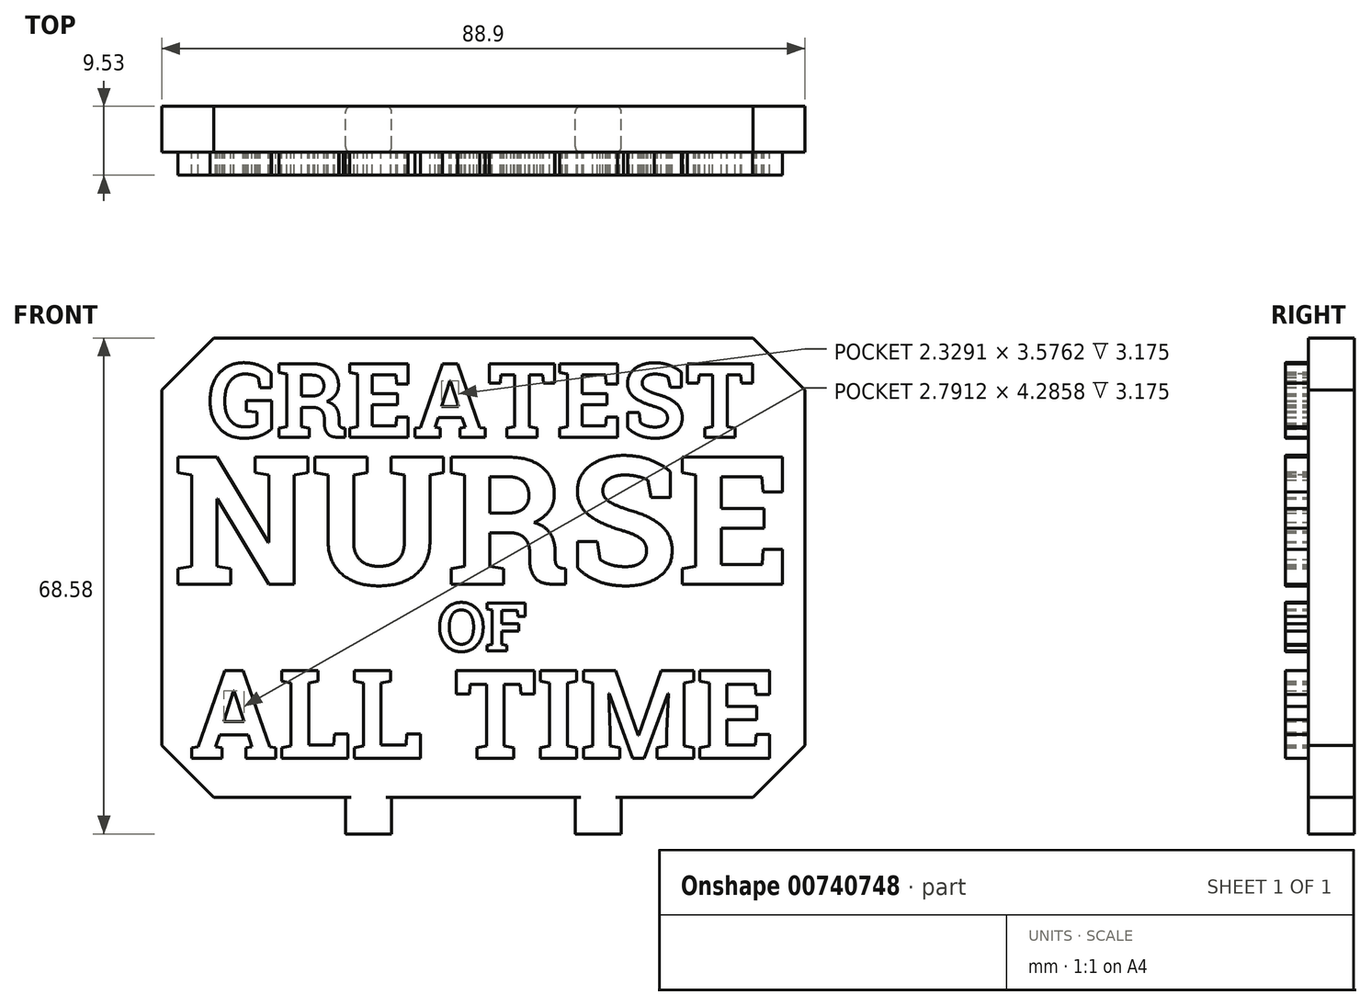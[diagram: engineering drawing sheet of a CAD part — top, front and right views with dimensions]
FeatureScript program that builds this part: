
annotation { "Feature Type Name" : "Feature", "Feature Type Description" : "" }
export const myFeature = defineFeature(function(context is Context, id is Id, definition is map)
    precondition{}
    {
        {
            var Q0;
            Q0=qCreatedBy(makeId("Front.planeOp"),FACE);
            var sketch = newSketch(context, id + "F0", { "sketchPlane" : qUnion([Q0])});
            skLineSegment(sketch, "E0.bottom", {"start": v(0, 0) * mm, "end": v(88.9, 0) * mm});
            skLineSegment(sketch, "E0.top", {"start": v(0, 63.5) * mm, "end": v(88.9, 63.5) * mm});
            skLineSegment(sketch, "E0.left", {"start": v(0, 0) * mm, "end": v(0, 63.5) * mm});
            skLineSegment(sketch, "E0.right", {"start": v(88.9, 0) * mm, "end": v(88.9, 63.5) * mm});
            skPoint(sketch, "E1", {"position": v(1.57, 38.36) * mm});
            skLineSegment(sketch, "E2", {"start": v(0, 56.32) * mm, "end": v(7.18, 63.5) * mm});
            skLineSegment(sketch, "E3", {"start": v(81.72, 63.5) * mm, "end": v(88.9, 56.32) * mm});
            skLineSegment(sketch, "E4", {"start": v(81.72, 0) * mm, "end": v(88.9, 7.18) * mm});
            skLineSegment(sketch, "E5", {"start": v(0, 7.18) * mm, "end": v(7.18, 0) * mm});
            skSolve(sketch);
        }
        {
            var Q0;
            {var subQ3=sQuery(id+"F0.wireOp",EDGE,"E2");Q0=makeQuery(id+"F0.imprint","IMPRINT",FACE,{"disambiguationData":[TD([[makeQuery(id+"F0.imprint","IMPRINT",EDGE,{"derivedFrom":subQ3}),-1.0]])]});}
            extrude(context, id + "F1", {"entities" : qUnion([Q0]), "depth" : 6.35 * mm, "offsetDistance" : 25.4 * mm});
        }
        {
            var Q0;
            Q0=makeQuery(id+"F1.opExtrude","CAP_FACE",FACE,{"disambiguationData":[OSD([sQuery(id+"F0.wireOp",EDGE,"E0.bottom"),sQuery(id+"F0.wireOp",EDGE,"E0.top"),sQuery(id+"F0.wireOp",EDGE,"E0.left"),sQuery(id+"F0.wireOp",EDGE,"E0.right"),sQuery(id+"F0.wireOp",EDGE,"E2"),sQuery(id+"F0.wireOp",EDGE,"E3"),sQuery(id+"F0.wireOp",EDGE,"E4"),sQuery(id+"F0.wireOp",EDGE,"E5")])],"isStart":false});
            var sketch = newSketch(context, id + "F2", { "sketchPlane" : qUnion([Q0])});
            skLineSegment(sketch, "E6.bottom", {"start": v(0, 0) * mm, "end": v(88.9, 0) * mm});
            skLineSegment(sketch, "E6.top", {"start": v(0, 63.5) * mm, "end": v(88.9, 63.5) * mm});
            skLineSegment(sketch, "E6.left", {"start": v(0, 0) * mm, "end": v(0, 63.5) * mm});
            skLineSegment(sketch, "E6.right", {"start": v(88.9, 0) * mm, "end": v(88.9, 63.5) * mm});
            skText(sketch, "E7", { "text": "GREATEST", "fontName": "RobotoSlab-Bold.ttf"});
            skText(sketch, "E8", { "text": "NURSE", "fontName": "RobotoSlab-Bold.ttf"});
            skText(sketch, "E9", { "text": "OF", "fontName": "RobotoSlab-Bold.ttf"});
            skText(sketch, "E10", { "text": "ALL TIME", "fontName": "RobotoSlab-Bold.ttf"});
            skPoint(sketch, "E11", {"position": v(1.57, 38.36) * mm});
            skLineSegment(sketch, "E12", {"start": v(0, 56.32) * mm, "end": v(7.18, 63.5) * mm});
            skLineSegment(sketch, "E13", {"start": v(81.72, 63.5) * mm, "end": v(88.9, 56.32) * mm});
            skLineSegment(sketch, "E14", {"start": v(81.72, 0) * mm, "end": v(88.9, 7.18) * mm});
            skLineSegment(sketch, "E15", {"start": v(0, 7.18) * mm, "end": v(7.18, 0) * mm});
            const initialGuessF2  = {"E7": [0.00635, 0.04979, 1, 0, 0.01028], "E8": [0.00157, 0.02947, 1, 0, 0.01778], "E9": [0.0381, 0.02021, 1, 0, 0.00672], "E10": [0.0038, 0.00535, 1, 0, 0.01232]};
            skSetInitialGuess(sketch, initialGuessF2);
            skSolve(sketch);
        }
        {
            var Q0;
            Q0=makeQuery(id+"F2.imprint","IMPRINT",FACE,{"disambiguationData":[TD([[makeQuery(id+"F2.imprint","IMPRINT",EDGE,{"derivedFrom":sQuery(id+"F2.wireOp",EDGE,"E7.sketch_text.stroke-0")}),-1.0]])]});
            var Q1;
            Q1=makeQuery(id+"F2.imprint","IMPRINT",FACE,{"disambiguationData":[TD([[makeQuery(id+"F2.imprint","IMPRINT",EDGE,{"derivedFrom":sQuery(id+"F2.wireOp",EDGE,"E7.sketch_text.stroke-26")}),-1.0]])]});
            var Q2;
            Q2=makeQuery(id+"F2.imprint","IMPRINT",FACE,{"disambiguationData":[TD([[makeQuery(id+"F2.imprint","IMPRINT",EDGE,{"derivedFrom":sQuery(id+"F2.wireOp",EDGE,"E7.sketch_text.stroke-62")}),-1.0]])]});
            var Q3;
            Q3=makeQuery(id+"F2.imprint","IMPRINT",FACE,{"disambiguationData":[TD([[makeQuery(id+"F2.imprint","IMPRINT",EDGE,{"derivedFrom":sQuery(id+"F2.wireOp",EDGE,"E7.sketch_text.stroke-83")}),-1.0]])]});
            var Q4;
            Q4=makeQuery(id+"F2.imprint","IMPRINT",FACE,{"disambiguationData":[TD([[makeQuery(id+"F2.imprint","IMPRINT",EDGE,{"derivedFrom":sQuery(id+"F2.wireOp",EDGE,"E7.sketch_text.stroke-103")}),-1.0]])]});
            var Q5;
            Q5=makeQuery(id+"F2.imprint","IMPRINT",FACE,{"disambiguationData":[TD([[makeQuery(id+"F2.imprint","IMPRINT",EDGE,{"derivedFrom":sQuery(id+"F2.wireOp",EDGE,"E7.sketch_text.stroke-119")}),-1.0]])]});
            var Q6;
            Q6=makeQuery(id+"F2.imprint","IMPRINT",FACE,{"disambiguationData":[TD([[makeQuery(id+"F2.imprint","IMPRINT",EDGE,{"derivedFrom":sQuery(id+"F2.wireOp",EDGE,"E7.sketch_text.stroke-140")}),-1.0]])]});
            var Q7;
            Q7=makeQuery(id+"F2.imprint","IMPRINT",FACE,{"disambiguationData":[TD([[makeQuery(id+"F2.imprint","IMPRINT",EDGE,{"derivedFrom":sQuery(id+"F2.wireOp",EDGE,"E7.sketch_text.stroke-170")}),-1.0]])]});
            var Q8;
            Q8=makeQuery(id+"F2.imprint","IMPRINT",FACE,{"disambiguationData":[TD([[makeQuery(id+"F2.imprint","IMPRINT",EDGE,{"derivedFrom":sQuery(id+"F2.wireOp",EDGE,"E8.sketch_text.stroke-0")}),-1.0]])]});
            var Q9;
            Q9=makeQuery(id+"F2.imprint","IMPRINT",FACE,{"disambiguationData":[TD([[makeQuery(id+"F2.imprint","IMPRINT",EDGE,{"derivedFrom":sQuery(id+"F2.wireOp",EDGE,"E8.sketch_text.stroke-24")}),-1.0]])]});
            var Q10;
            Q10=makeQuery(id+"F2.imprint","IMPRINT",FACE,{"disambiguationData":[TD([[makeQuery(id+"F2.imprint","IMPRINT",EDGE,{"derivedFrom":sQuery(id+"F2.wireOp",EDGE,"E8.sketch_text.stroke-48")}),-1.0]])]});
            var Q11;
            Q11=makeQuery(id+"F2.imprint","IMPRINT",FACE,{"disambiguationData":[TD([[makeQuery(id+"F2.imprint","IMPRINT",EDGE,{"derivedFrom":sQuery(id+"F2.wireOp",EDGE,"E8.sketch_text.stroke-84")}),-1.0]])]});
            var Q12;
            Q12=makeQuery(id+"F2.imprint","IMPRINT",FACE,{"disambiguationData":[TD([[makeQuery(id+"F2.imprint","IMPRINT",EDGE,{"derivedFrom":sQuery(id+"F2.wireOp",EDGE,"E8.sketch_text.stroke-114")}),-1.0]])]});
            var Q13;
            Q13=makeQuery(id+"F2.imprint","IMPRINT",FACE,{"disambiguationData":[TD([[makeQuery(id+"F2.imprint","IMPRINT",EDGE,{"derivedFrom":sQuery(id+"F2.wireOp",EDGE,"E9.sketch_text.stroke-0")}),-1.0]])]});
            var Q14;
            Q14=makeQuery(id+"F2.imprint","IMPRINT",FACE,{"disambiguationData":[TD([[makeQuery(id+"F2.imprint","IMPRINT",EDGE,{"derivedFrom":sQuery(id+"F2.wireOp",EDGE,"E9.sketch_text.stroke-20")}),-1.0]])]});
            var Q15;
            Q15=makeQuery(id+"F2.imprint","IMPRINT",FACE,{"disambiguationData":[TD([[makeQuery(id+"F2.imprint","IMPRINT",EDGE,{"derivedFrom":sQuery(id+"F2.wireOp",EDGE,"E10.sketch_text.stroke-0")}),-1.0]])]});
            var Q16;
            Q16=makeQuery(id+"F2.imprint","IMPRINT",FACE,{"disambiguationData":[TD([[makeQuery(id+"F2.imprint","IMPRINT",EDGE,{"derivedFrom":sQuery(id+"F2.wireOp",EDGE,"E10.sketch_text.stroke-20")}),-1.0]])]});
            var Q17;
            Q17=makeQuery(id+"F2.imprint","IMPRINT",FACE,{"disambiguationData":[TD([[makeQuery(id+"F2.imprint","IMPRINT",EDGE,{"derivedFrom":sQuery(id+"F2.wireOp",EDGE,"E10.sketch_text.stroke-36")}),-1.0]])]});
            var Q18;
            Q18=makeQuery(id+"F2.imprint","IMPRINT",FACE,{"disambiguationData":[TD([[makeQuery(id+"F2.imprint","IMPRINT",EDGE,{"derivedFrom":sQuery(id+"F2.wireOp",EDGE,"E10.sketch_text.stroke-52")}),-1.0]])]});
            var Q19;
            Q19=makeQuery(id+"F2.imprint","IMPRINT",FACE,{"disambiguationData":[TD([[makeQuery(id+"F2.imprint","IMPRINT",EDGE,{"derivedFrom":sQuery(id+"F2.wireOp",EDGE,"E10.sketch_text.stroke-68")}),-1.0]])]});
            var Q20;
            Q20=makeQuery(id+"F2.imprint","IMPRINT",FACE,{"disambiguationData":[TD([[makeQuery(id+"F2.imprint","IMPRINT",EDGE,{"derivedFrom":sQuery(id+"F2.wireOp",EDGE,"E10.sketch_text.stroke-80")}),-1.0]])]});
            var Q21;
            Q21=makeQuery(id+"F2.imprint","IMPRINT",FACE,{"disambiguationData":[TD([[makeQuery(id+"F2.imprint","IMPRINT",EDGE,{"derivedFrom":sQuery(id+"F2.wireOp",EDGE,"E10.sketch_text.stroke-111")}),-1.0]])]});
            extrude(context, id + "F3", {"entities" : qUnion([Q0, Q1, Q2, Q3, Q4, Q5, Q6, Q7, Q8, Q9, Q10, Q11, Q12, Q13, Q14, Q15, Q16, Q17, Q18, Q19, Q20, Q21]), "operationType" : NewBodyOperationType.ADD, "surfaceOperationType" : NewSurfaceOperationType.ADD, "depth" : 3.17 * mm, "offsetDistance" : 25.4 * mm});
        }
        {
            var Q0;
            Q0=makeQuery(id+"F1.opExtrude","SWEPT_FACE",FACE,{"disambiguationData":[OSD([sQuery(id+"F0.wireOp",EDGE,"E0.bottom")])]});
            var sketch = newSketch(context, id + "F4", { "sketchPlane" : qUnion([Q0])});
            skLineSegment(sketch, "E16.bottom", {"start": v(25.4, 6.35) * mm, "end": v(31.75, 6.35) * mm});
            skLineSegment(sketch, "E16.top", {"start": v(25.4, 0) * mm, "end": v(31.75, 0) * mm});
            skLineSegment(sketch, "E16.left", {"start": v(25.4, 6.35) * mm, "end": v(25.4, 0) * mm});
            skLineSegment(sketch, "E16.right", {"start": v(31.75, 6.35) * mm, "end": v(31.75, 0) * mm});
            skLineSegment(sketch, "E17.bottom", {"start": v(57.15, 6.35) * mm, "end": v(63.5, 6.35) * mm});
            skLineSegment(sketch, "E17.top", {"start": v(57.15, 0) * mm, "end": v(63.5, 0) * mm});
            skLineSegment(sketch, "E17.left", {"start": v(57.15, 6.35) * mm, "end": v(57.15, 0) * mm});
            skLineSegment(sketch, "E17.right", {"start": v(63.5, 6.35) * mm, "end": v(63.5, 0) * mm});
            skSolve(sketch);
        }
        {
            var Q0;
            Q0=makeQuery(id+"F4.imprint","IMPRINT",FACE,{"disambiguationData":[TD([[makeQuery(id+"F4.imprint","IMPRINT",EDGE,{"derivedFrom":sQuery(id+"F4.wireOp",EDGE,"E16.bottom")}),-1.0]])]});
            var Q1;
            Q1=makeQuery(id+"F4.imprint","IMPRINT",FACE,{"disambiguationData":[TD([[makeQuery(id+"F4.imprint","IMPRINT",EDGE,{"derivedFrom":sQuery(id+"F4.wireOp",EDGE,"E17.bottom")}),-1.0]])]});
            extrude(context, id + "F5", {"entities" : qUnion([Q0, Q1]), "operationType" : NewBodyOperationType.ADD, "depth" : 5.08 * mm, "offsetDistance" : 25.4 * mm});
        }
        {
            var Q0;
            Q0=makeQuery(id+"F5.opExtrude","SWEPT_EDGE",EDGE,{"disambiguationData":[OSD([sQuery(id+"F0.wireOp",EDGE,"E0.bottom"),sQuery(id+"F4.wireOp",EDGE,"E16.bottom"),sQuery(id+"F4.wireOp",EDGE,"E16.left")])]});
            var Q1;
            Q1=makeQuery(id+"F5.opExtrude","SWEPT_EDGE",EDGE,{"disambiguationData":[OSD([sQuery(id+"F0.wireOp",EDGE,"E0.bottom"),sQuery(id+"F4.wireOp",EDGE,"E16.top"),sQuery(id+"F4.wireOp",EDGE,"E16.left")])]});
            var Q2;
            Q2=makeQuery(id+"F5.opExtrude","SWEPT_EDGE",EDGE,{"disambiguationData":[OSD([sQuery(id+"F0.wireOp",EDGE,"E0.bottom"),sQuery(id+"F4.wireOp",EDGE,"E16.top"),sQuery(id+"F4.wireOp",EDGE,"E16.right")])]});
            var Q3;
            Q3=makeQuery(id+"F5.opExtrude","SWEPT_EDGE",EDGE,{"disambiguationData":[OSD([sQuery(id+"F0.wireOp",EDGE,"E0.bottom"),sQuery(id+"F4.wireOp",EDGE,"E16.bottom"),sQuery(id+"F4.wireOp",EDGE,"E16.right")])]});
            var Q4;
            Q4=makeQuery(id+"F5.opExtrude","SWEPT_EDGE",EDGE,{"disambiguationData":[OSD([sQuery(id+"F0.wireOp",EDGE,"E0.bottom"),sQuery(id+"F4.wireOp",EDGE,"E17.bottom"),sQuery(id+"F4.wireOp",EDGE,"E17.left")])]});
            var Q5;
            Q5=makeQuery(id+"F5.opExtrude","SWEPT_EDGE",EDGE,{"disambiguationData":[OSD([sQuery(id+"F0.wireOp",EDGE,"E0.bottom"),sQuery(id+"F4.wireOp",EDGE,"E17.top"),sQuery(id+"F4.wireOp",EDGE,"E17.left")])]});
            var Q6;
            Q6=makeQuery(id+"F5.opExtrude","SWEPT_EDGE",EDGE,{"disambiguationData":[OSD([sQuery(id+"F0.wireOp",EDGE,"E0.bottom"),sQuery(id+"F4.wireOp",EDGE,"E17.top"),sQuery(id+"F4.wireOp",EDGE,"E17.right")])]});
            var Q7;
            Q7=makeQuery(id+"F5.opExtrude","SWEPT_EDGE",EDGE,{"disambiguationData":[OSD([sQuery(id+"F0.wireOp",EDGE,"E0.bottom"),sQuery(id+"F4.wireOp",EDGE,"E17.bottom"),sQuery(id+"F4.wireOp",EDGE,"E17.right")])]});
            fillet(context, id + "F6", {"entities" : qUnion([Q0, Q1, Q2, Q3, Q4, Q5, Q6, Q7]), "radius" : 0.76 * mm, "tangentPropagation" : true, "allowEdgeOverflow" : false});
        }
    });
